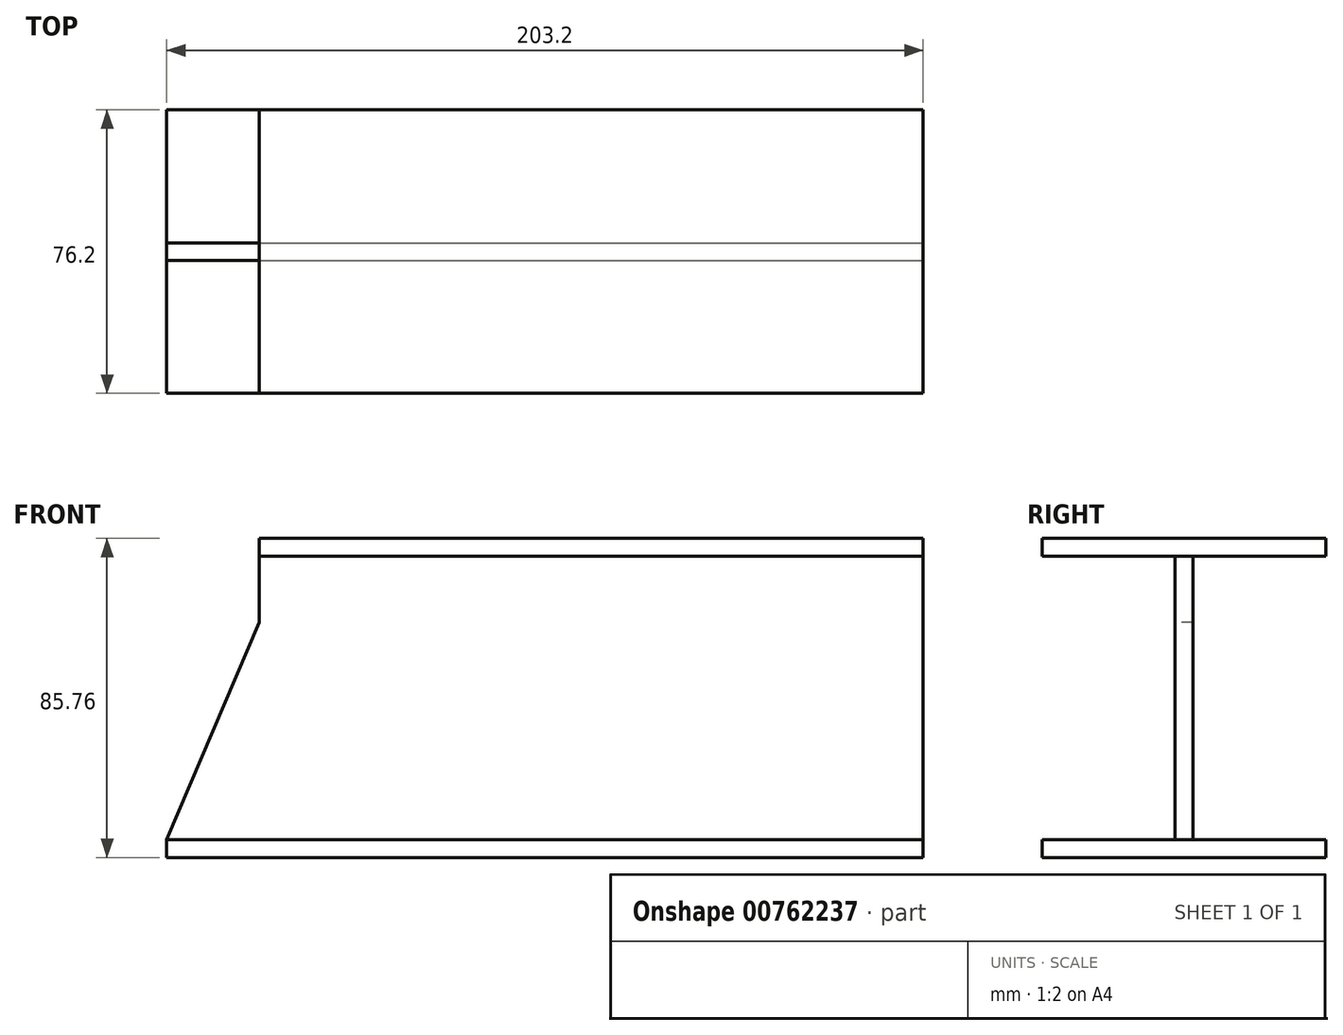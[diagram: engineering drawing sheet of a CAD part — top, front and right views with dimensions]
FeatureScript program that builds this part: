
annotation { "Feature Type Name" : "Feature", "Feature Type Description" : "" }
export const myFeature = defineFeature(function(context is Context, id is Id, definition is map)
    precondition{}
    {
        {
            var Q0;
            Q0=qCreatedBy(makeId("Front.planeOp"),FACE);
            var sketch = newSketch(context, id + "F0", { "sketchPlane" : qUnion([Q0])});
            skLineSegment(sketch, "E0.bottom", {"start": v(0, 0) * mm, "end": v(203.2, 0) * mm});
            skLineSegment(sketch, "E0.top", {"start": v(0, 76.2) * mm, "end": v(203.2, 76.2) * mm});
            skLineSegment(sketch, "E0.left", {"start": v(0, 0) * mm, "end": v(0, 76.2) * mm});
            skLineSegment(sketch, "E0.right", {"start": v(203.2, 0) * mm, "end": v(203.2, 76.2) * mm});
            skSolve(sketch);
        }
        {
            var Q0;
            Q0=makeQuery(id+"F0.imprint","IMPRINT",FACE,{"disambiguationData":[TD([[makeQuery(id+"F0.imprint","IMPRINT",EDGE,{"derivedFrom":sQuery(id+"F0.wireOp",EDGE,"E0.bottom")}),1.0]])]});
            extrude(context, id + "F1", {"entities" : qUnion([Q0]), "depth" : 4.78 * mm, "offsetDistance" : 25.4 * mm});
        }
        {
            var Q0;
            Q0=qCreatedBy(makeId("Right.planeOp"),FACE);
            var sketch = newSketch(context, id + "F2", { "sketchPlane" : qUnion([Q0])});
            skLineSegment(sketch, "E1.bottom", {"start": v(-40.49, 76.2) * mm, "end": v(35.71, 76.2) * mm});
            skLineSegment(sketch, "E1.top", {"start": v(-40.49, 80.98) * mm, "end": v(35.71, 80.98) * mm});
            skLineSegment(sketch, "E1.left", {"start": v(-40.49, 76.2) * mm, "end": v(-40.49, 80.98) * mm});
            skLineSegment(sketch, "E1.right", {"start": v(35.71, 76.2) * mm, "end": v(35.71, 80.98) * mm});
            skPoint(sketch, "E2", {"position": v(-2.39, 76.2) * mm});
            skLineSegment(sketch, "E3.bottom", {"start": v(-40.49, -4.78) * mm, "end": v(35.71, -4.78) * mm});
            skLineSegment(sketch, "E3.top", {"start": v(-40.49, 0) * mm, "end": v(35.71, 0) * mm});
            skLineSegment(sketch, "E3.left", {"start": v(-40.49, -4.78) * mm, "end": v(-40.49, 0) * mm});
            skLineSegment(sketch, "E3.right", {"start": v(35.71, -4.78) * mm, "end": v(35.71, 0) * mm});
            skPoint(sketch, "E4", {"position": v(-2.39, 0) * mm});
            skSolve(sketch);
        }
        {
            var Q0;
            Q0=makeQuery(id+"F2.imprint","IMPRINT",FACE,{"disambiguationData":[TD([[makeQuery(id+"F2.imprint","IMPRINT",EDGE,{"derivedFrom":sQuery(id+"F2.wireOp",EDGE,"E1.bottom")}),1.0]])]});
            var Q1;
            Q1=makeQuery(id+"F2.imprint","IMPRINT",FACE,{"disambiguationData":[TD([[makeQuery(id+"F2.imprint","IMPRINT",EDGE,{"derivedFrom":sQuery(id+"F2.wireOp",EDGE,"E3.bottom")}),1.0]])]});
            extrude(context, id + "F3", {"entities" : qUnion([Q0, Q1]), "depth" : 203.2 * mm, "offsetDistance" : 25.4 * mm});
        }
        {
            var Q0;
            Q0=makeQuery(id+"F3.opExtrude","SWEPT_FACE",FACE,{"disambiguationData":[OSD([sQuery(id+"F2.wireOp",EDGE,"E1.left")])]});
            var sketch = newSketch(context, id + "F4", { "sketchPlane" : qUnion([Q0])});
            skLineSegment(sketch, "E5", {"start": v(0, 0) * mm, "end": v(24.9, 58.41) * mm});
            skLineSegment(sketch, "E6", {"start": v(24.9, 58.41) * mm, "end": v(24.9, 80.98) * mm});
            skLineSegment(sketch, "E7", {"start": v(24.9, 80.98) * mm, "end": v(0, 80.98) * mm});
            skLineSegment(sketch, "E8", {"start": v(0, 80.98) * mm, "end": v(0, 0) * mm});
            skSolve(sketch);
        }
        {
            var Q0;
            {var subQ0=sQuery(id+"F4.wireOp",EDGE,"E5");Q0=makeQuery(id+"F4.imprint","IMPRINT",FACE,{"disambiguationData":[TD([[makeQuery(id+"F4.imprint","IMPRINT",EDGE,{"derivedFrom":subQ0}),1.0]])]});}
            var Q1;
            {var subQ0=sQuery(id+"F4.wireOp",EDGE,"E7");Q1=makeQuery(id+"F4.imprint","IMPRINT",FACE,{"disambiguationData":[TD([[makeQuery(id+"F4.imprint","IMPRINT",EDGE,{"derivedFrom":subQ0}),1.0]])]});}
            extrude(context, id + "F5", {"entities" : qUnion([Q0, Q1]), "operationType" : NewBodyOperationType.REMOVE, "oppositeDirection" : true, "depth" : 80.26 * mm, "offsetDistance" : 25.4 * mm});
        }
    });
